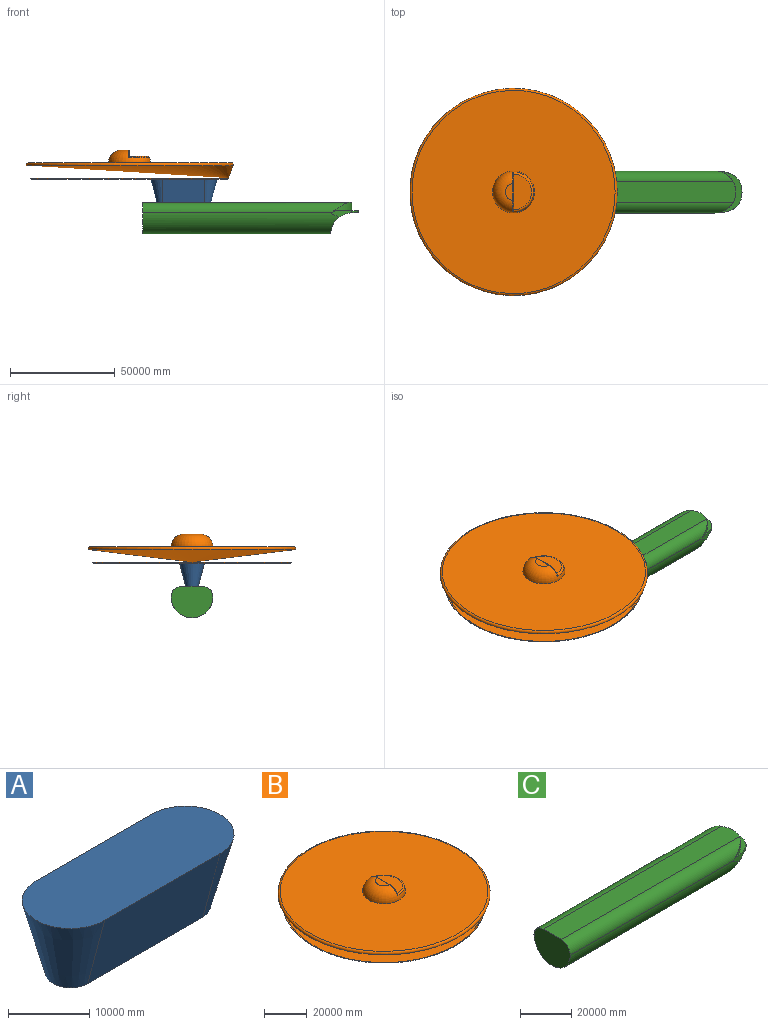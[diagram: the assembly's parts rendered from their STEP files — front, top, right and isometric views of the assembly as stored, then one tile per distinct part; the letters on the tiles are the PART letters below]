
ASSEMBLY  parts=3 mates=2
PART A: 6 faces, bbox 31894.9x11894.9x11000 mm
  f0: plane 26000x6000mm, normal (0,0,-1), area 148274333.9mm2, adj f1,f2,f4,f5
  f1: cone r=3000mm half-angle=15deg, axis (0,0,1), area 160054405.7mm2, adj f0,f2,f3,f4
  f2: plane 20000x11000mm, normal (0,-0.97,-0.26), area 227760759.7mm2, adj f0,f1,f3,f5
  f3: plane 31894.88x11894.88mm, normal (0,0,1), area 349022235.4mm2, adj f1,f2,f4,f5
  f4: plane 20000x11000mm, normal (0,0.97,-0.26), area 227760759.7mm2, adj f0,f1,f3,f5
  f5: cone r=3000mm half-angle=15deg, axis (0,0,1), area 160054405.7mm2, adj f0,f2,f3,f4
PART B: 13 faces, bbox 107312.4x107312.4x14000.5 mm
  f0: plane 17190.7x2500.13mm, normal (1,0,0), area 36146617.2mm2, adj f5,f9,f10,f11,f12
  f1: plane 97143.7x97143.7mm, normal (0,0,1), area 7097564053.4mm2, adj f7,f8
  f2: cone r=50000mm half-angle=20deg, axis (0,0,1), area 1942525836.6mm2, adj f6,f7
  f3: plane 92776.06x92776.06mm, normal (0,0,-1), area 6760234209.6mm2, adj f6
  f4: plane 7937.25x3500mm, normal (0,0,1), area 21143182.4mm2, adj f8,f10
  f5: plane 17165.15x8582.58mm, normal (0,0,1), area 115705808.6mm2, adj f0,f12
  f6: torus R=46388.03mm, axis (0,0,1), area 360225384.7mm2, adj f2,f3
  f7: torus R=48571.85mm, axis (0,0,1), area 594347117.4mm2, adj f1,f2
  f8: torus R=4000mm, axis (0,0,1), area 300591380.6mm2, adj f1,f4,f9,f11,f12
  f9: bspline ~5743.32x3862.02mm, area 5047374.2mm2, adj f0,f8,f10,f12
  f10: cylinder r=500mm len=7937.25mm, axis (0,-1,0), area 6233904.7mm2, adj f0,f4,f9,f11
  f11: bspline ~5743.32x3862.02mm, area 5047374.2mm2, adj f0,f8,f10,f12
  f12: torus R=8582.58mm, axis (0,0,1), area 33603018.9mm2, adj f0,f5,f8,f9,f11
PART C: 13 faces, bbox 103000x20000x15000 mm
  f0: cylinder r=10000mm len=93746.15mm, axis (-1,0,0), area 2856034980.7mm2, adj f1,f2,f5,f7,f10,f11
  f1: cylinder r=5000mm len=98660.25mm, axis (-1,0,0), area 745969755.1mm2, adj f0,f3,f6,f7,f8,f11
  f2: cylinder r=10000mm len=19511.42mm, axis (0,1,0), area 254629402.9mm2, adj f0,f4,f10,f11
  f3: plane 20000x11582.18mm, normal (0,0,1), area 59439479.1mm2, adj f1,f5,f8,f9,f10,f11,f12
  f4: plane 14599.99x3000mm, normal (0,0,-1), area 31507680mm2, adj f2,f9,f12
  f5: cylinder r=5000mm len=98660.25mm, axis (-1,0,0), area 745969307.2mm2, adj f0,f3,f6,f7,f8,f10
  f6: plane 100000x10000mm, normal (0,0,1), area 995661147.8mm2, adj f1,f5,f7,f8
  f7: plane 20000x15000mm, normal (-1,0,0), area 246349540.8mm2, adj f0,f1,f5,f6
  f8: cylinder r=10000mm len=19797.96mm, axis (0,0,1), area 87421177.4mm2, adj f1,f3,f5,f6
  f9: extruded ~7300x3000mm, area 8167815.2mm2, adj f3,f4,f10,f12
  f10: extruded ~10000x3196.84mm, area 17827884.3mm2, adj f0,f2,f3,f5,f9
  f11: extruded ~10000x3196.84mm, area 17827884.3mm2, adj f0,f1,f2,f3,f12
  f12: extruded ~7300x3000mm, area 8167815.2mm2, adj f3,f4,f9,f11
PLACE A t=(-101557.87,-38816.36,-4654.4)mm
PLACE B t=(-98211.68,-38816.36,-4654.4)mm
PLACE C t=(-102695.52,-38816.36,-4654.4)mm
MATE fastened A.f3 <-> B.f3  axis (0,0,1) through (-72211.68,-38816.36,-4654.4)mm
MATE fastened A.f0 <-> C.f6  axis (0,0,-1) through (-72211.68,-38816.36,-15654.4)mm
